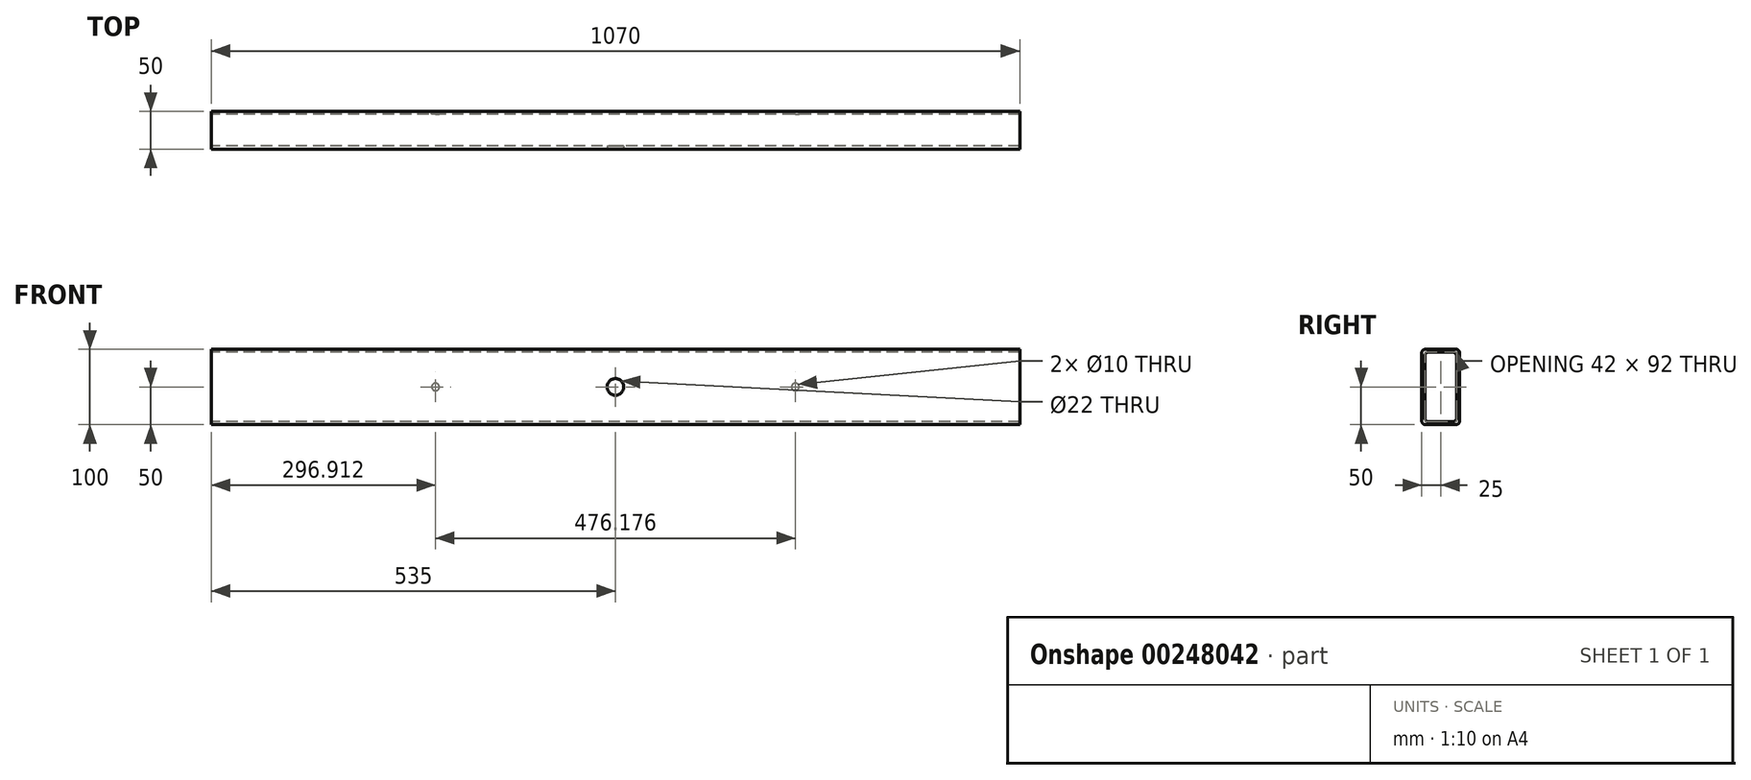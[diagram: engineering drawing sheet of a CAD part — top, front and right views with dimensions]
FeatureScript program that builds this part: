
annotation { "Feature Type Name" : "Feature", "Feature Type Description" : "" }
export const myFeature = defineFeature(function(context is Context, id is Id, definition is map)
    precondition{}
    {
        {
            var Q0;
            Q0=qCreatedBy(makeId("Front.planeOp"),FACE);
            var sketch = newSketch(context, id + "F0", { "sketchPlane" : qUnion([Q0])});
            skLineSegment(sketch, "E0.bottom", {"start": v(535, -50) * mm, "end": v(-535, -50) * mm});
            skLineSegment(sketch, "E0.top", {"start": v(535, 50) * mm, "end": v(-535, 50) * mm});
            skLineSegment(sketch, "E0.left", {"start": v(535, -50) * mm, "end": v(535, 50) * mm});
            skLineSegment(sketch, "E0.right", {"start": v(-535, -50) * mm, "end": v(-535, 50) * mm});
            skPoint(sketch, "E0.middle", {"position": v(0, 0) * mm});
            skSolve(sketch);
        }
        {
            var Q0;
            Q0=makeQuery(id+"F0.imprint","IMPRINT",FACE,{"disambiguationData":[TD([[makeQuery(id+"F0.imprint","IMPRINT",EDGE,{"derivedFrom":sQuery(id+"F0.wireOp",EDGE,"E0.bottom")}),-1.0]])]});
            extrude(context, id + "F1", {"entities" : qUnion([Q0]), "depth" : 50 * mm});
        }
        {
            var Q0;
            Q0=makeQuery(id+"F1.opExtrude","SWEPT_FACE",FACE,{"disambiguationData":[OSD([sQuery(id+"F0.wireOp",EDGE,"E0.right")])]});
            var Q1;
            Q1=makeQuery(id+"F1.opExtrude","SWEPT_FACE",FACE,{"disambiguationData":[OSD([sQuery(id+"F0.wireOp",EDGE,"E0.left")])]});
            var Q2;
            Q2=makeQuery(id+"F1.opExtrude","SWEPT_BODY",BODY,{"disambiguationData":[OSD([sQuery(id+"F0.wireOp",EDGE,"E0.bottom"),sQuery(id+"F0.wireOp",EDGE,"E0.top"),sQuery(id+"F0.wireOp",EDGE,"E0.left"),sQuery(id+"F0.wireOp",EDGE,"E0.right")])]});
            shell(context, id + "F2", {"entities" : qUnion([Q0, Q1]), "parts" : qUnion([Q2]), "thickness" : 4 * mm});
        }
        {
            var Q0;
            {var subQ0=sQuery(id+"F0.wireOp",EDGE,"E0.top");Q0=makeQuery(id+"F2.opShell","OFFSET_EDGE",EDGE,{"disambiguationData":[OSD([subQ0]),TDD([makeQuery(id+"F1.opExtrude","CAP_EDGE",EDGE,{"disambiguationData":[OSD([subQ0])],"isStart":false})])]});}
            var Q1;
            {var subQ0=sQuery(id+"F0.wireOp",EDGE,"E0.top");Q1=makeQuery(id+"F2.opShell","OFFSET_EDGE",EDGE,{"disambiguationData":[OSD([subQ0]),TDD([makeQuery(id+"F1.opExtrude","CAP_EDGE",EDGE,{"disambiguationData":[OSD([subQ0])],"isStart":true})])]});}
            var Q2;
            {var subQ0=sQuery(id+"F0.wireOp",EDGE,"E0.bottom");Q2=makeQuery(id+"F2.opShell","OFFSET_EDGE",EDGE,{"disambiguationData":[OSD([subQ0]),TDD([makeQuery(id+"F1.opExtrude","CAP_EDGE",EDGE,{"disambiguationData":[OSD([subQ0])],"isStart":false})])]});}
            var Q3;
            {var subQ0=sQuery(id+"F0.wireOp",EDGE,"E0.bottom");Q3=makeQuery(id+"F2.opShell","OFFSET_EDGE",EDGE,{"disambiguationData":[OSD([subQ0]),TDD([makeQuery(id+"F1.opExtrude","CAP_EDGE",EDGE,{"disambiguationData":[OSD([subQ0])],"isStart":true})])]});}
            var Q4;
            Q4=makeQuery(id+"F1.opExtrude","CAP_EDGE",EDGE,{"disambiguationData":[OSD([sQuery(id+"F0.wireOp",EDGE,"E0.bottom")])],"isStart":false});
            var Q5;
            Q5=makeQuery(id+"F1.opExtrude","CAP_EDGE",EDGE,{"disambiguationData":[OSD([sQuery(id+"F0.wireOp",EDGE,"E0.top")])],"isStart":false});
            var Q6;
            Q6=makeQuery(id+"F1.opExtrude","CAP_EDGE",EDGE,{"disambiguationData":[OSD([sQuery(id+"F0.wireOp",EDGE,"E0.top")])],"isStart":true});
            var Q7;
            Q7=makeQuery(id+"F1.opExtrude","CAP_EDGE",EDGE,{"disambiguationData":[OSD([sQuery(id+"F0.wireOp",EDGE,"E0.bottom")])],"isStart":true});
            fillet(context, id + "F3", {"entities" : qUnion([Q0, Q1, Q2, Q3, Q4, Q5, Q6, Q7]), "radius" : 5 * mm, "tangentPropagation" : true, "allowEdgeOverflow" : false});
        }
        {
            var Q0;
            Q0=makeQuery(id+"F1.opExtrude","CAP_FACE",FACE,{"disambiguationData":[OSD([sQuery(id+"F0.wireOp",EDGE,"E0.bottom"),sQuery(id+"F0.wireOp",EDGE,"E0.top"),sQuery(id+"F0.wireOp",EDGE,"E0.left"),sQuery(id+"F0.wireOp",EDGE,"E0.right")])],"isStart":false});
            var sketch = newSketch(context, id + "F4", { "sketchPlane" : qUnion([Q0])});
            skPoint(sketch, "E1", {"position": v(0, 0) * mm});
            skSolve(sketch);
        }
        {
            var Q0;
            Q0=sQuery(id+"F4.wireOp",VERTEX,"E1");
            var Q1;
            Q1=makeQuery(id+"F1.opExtrude","SWEPT_BODY",BODY,{"disambiguationData":[OSD([sQuery(id+"F0.wireOp",EDGE,"E0.bottom"),sQuery(id+"F0.wireOp",EDGE,"E0.top"),sQuery(id+"F0.wireOp",EDGE,"E0.left"),sQuery(id+"F0.wireOp",EDGE,"E0.right")])]});
            hole(context, id + "F5", {"style" : HoleStyle.SIMPLE, "endStyle" : HoleEndStyle.BLIND, "holeDiameter" : 22 * mm, "holeDepth" : 4 * mm, "tappedDepth" : 12 * mm, "tapClearance" : 3, "locations" : qUnion([Q0]), "scope" : qUnion([Q1])});
        }
        {
            var Q0;
            Q0=makeQuery(id+"F1.opExtrude","CAP_FACE",FACE,{"disambiguationData":[OSD([sQuery(id+"F0.wireOp",EDGE,"E0.bottom"),sQuery(id+"F0.wireOp",EDGE,"E0.top"),sQuery(id+"F0.wireOp",EDGE,"E0.left"),sQuery(id+"F0.wireOp",EDGE,"E0.right")])],"isStart":true});
            var sketch = newSketch(context, id + "F6", { "sketchPlane" : qUnion([Q0])});
            skPoint(sketch, "E2", {"position": v(238.09, -103.06) * mm});
            skPoint(sketch, "E3", {"position": v(238.09, 0) * mm});
            skPoint(sketch, "E4", {"position": v(-238.09, 0) * mm});
            skSolve(sketch);
        }
        {
            var Q0;
            Q0=sQuery(id+"F6.wireOp",VERTEX,"E3");
            var Q1;
            Q1=sQuery(id+"F6.wireOp",VERTEX,"E4");
            var Q2;
            Q2=makeQuery(id+"F1.opExtrude","SWEPT_BODY",BODY,{"disambiguationData":[OSD([sQuery(id+"F0.wireOp",EDGE,"E0.bottom"),sQuery(id+"F0.wireOp",EDGE,"E0.top"),sQuery(id+"F0.wireOp",EDGE,"E0.left"),sQuery(id+"F0.wireOp",EDGE,"E0.right")])]});
            hole(context, id + "F7", {"style" : HoleStyle.SIMPLE, "endStyle" : HoleEndStyle.BLIND, "standardTappedOrClearance" : lookupTablePath({ "standard" : "ISO", "size" : "10", "type" : "Drilled" }), "standardBlindInLast" : lookupTablePath({ "standard" : "ISO", "size" : "10", "type" : "Drilled" }), "holeDiameter" : 10 * mm, "majorDiameter" : 5 * mm, "holeDepth" : 5 * mm, "tappedDepth" : 12 * mm, "tapClearance" : 3, "locations" : qUnion([Q0, Q1]), "scope" : qUnion([Q2])});
        }
    });
